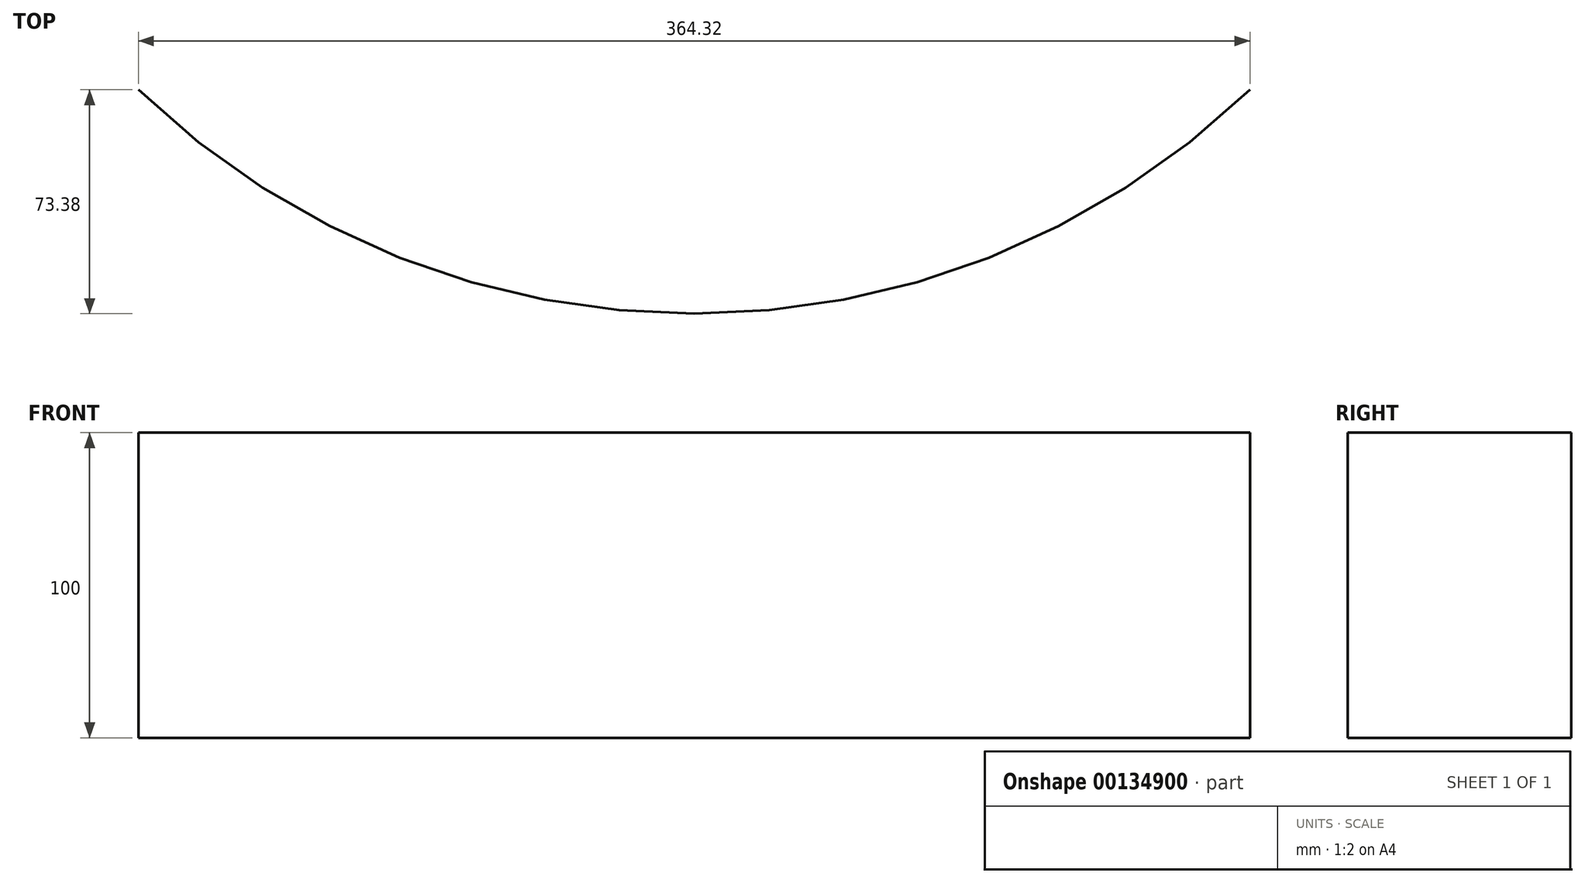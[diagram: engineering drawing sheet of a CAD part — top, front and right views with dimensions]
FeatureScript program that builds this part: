
annotation { "Feature Type Name" : "Feature", "Feature Type Description" : "" }
export const myFeature = defineFeature(function(context is Context, id is Id, definition is map)
    precondition{}
    {
        {
            var Q0;
            Q0=qCreatedBy(makeId("Top.planeOp"),FACE);
            var sketch = newSketch(context, id + "F0", { "sketchPlane" : qUnion([Q0])});
            skArc(sketch, "E0", {"start": v(-182.16, -189.43) * mm, "mid": v(0, -262.8) * mm, "end": v(182.16, -189.43) * mm});
            skLineSegment(sketch, "E1", {"start": v(-182.16, -189.43) * mm, "end": v(182.16, -189.43) * mm, "construction": true});
            skLineSegment(sketch, "E2", {"start": v(-7.5, -262.7) * mm, "end": v(-7.5, -285.52) * mm});
            skSolve(sketch);
        }
        {
            var Q0;
            Q0=qSketchRegion(id+"F0",true);
            var Q1;
            Q1=sQuery(id+"F0.wireOp",EDGE,"E0");
            extrude(context, id + "F1", {"entities" : qUnion([Q0]), "bodyType" : ToolBodyType.SURFACE, "surfaceEntities" : qUnion([Q1]), "oppositeDirection" : true, "depth" : 100 * mm});
        }
    });
